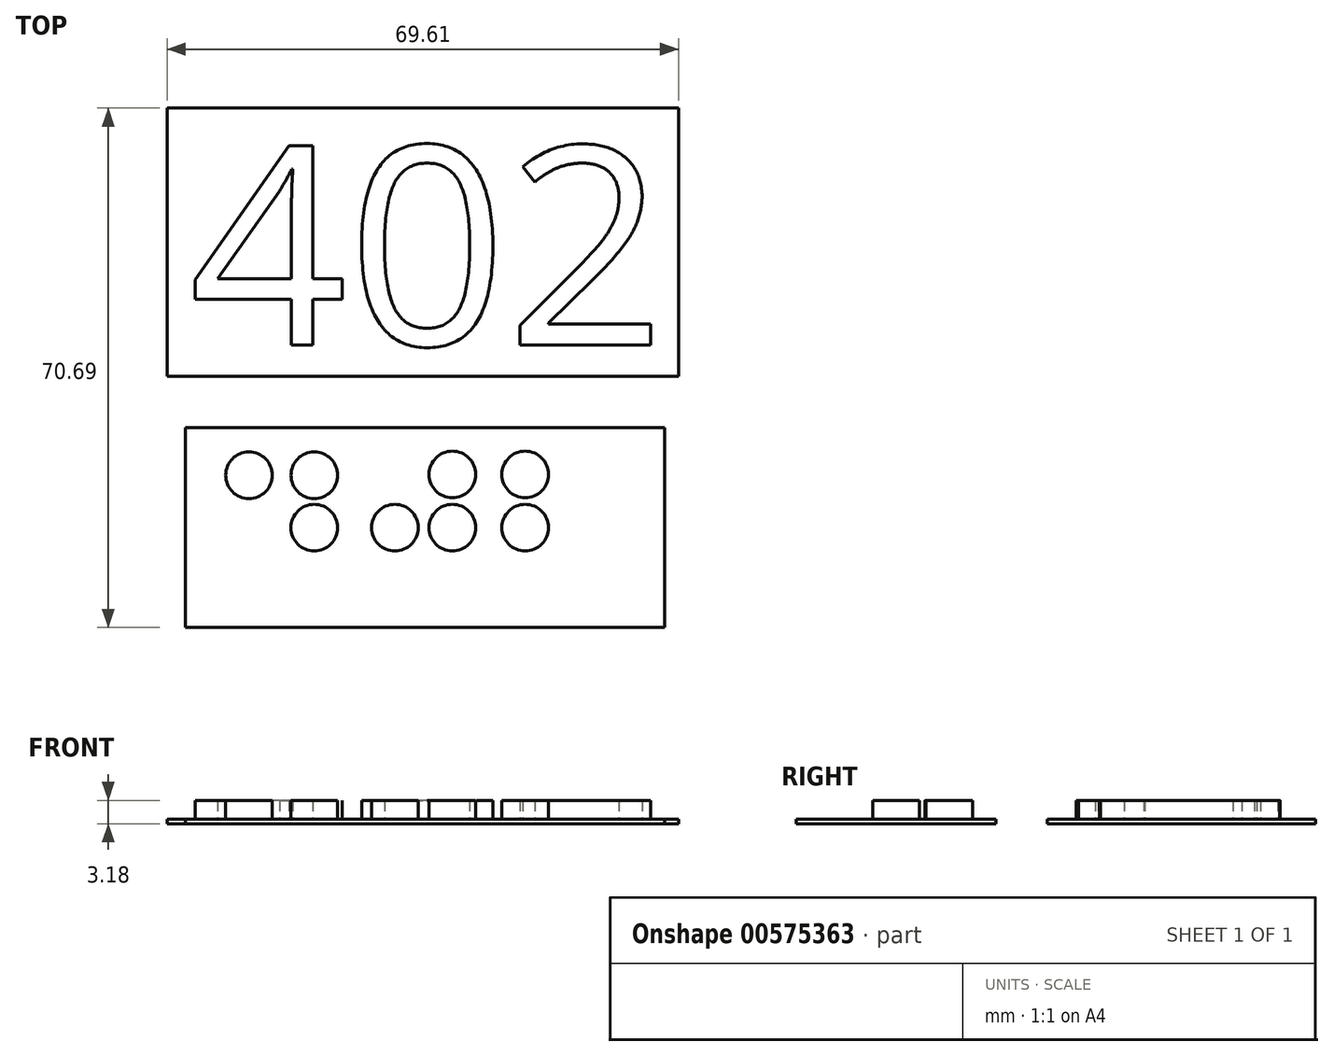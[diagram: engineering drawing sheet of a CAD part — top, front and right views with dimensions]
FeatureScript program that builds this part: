
annotation { "Feature Type Name" : "Feature", "Feature Type Description" : "" }
export const myFeature = defineFeature(function(context is Context, id is Id, definition is map)
    precondition{}
    {
        {
            var Q0;
            Q0=qCreatedBy(makeId("Top.planeOp"),FACE);
            var sketch = newSketch(context, id + "F0", { "sketchPlane" : qUnion([Q0])});
            skText(sketch, "E0", { "text": "402\n", "fontName": "OpenSans-Regular.ttf"});
            skCircle(sketch, "E1", {"center": v(-65.38, 7.14) * mm, "radius": 3.18 * mm});
            skCircle(sketch, "E2", {"center": v(-27.8, 7.24) * mm, "radius": 3.18 * mm});
            skCircle(sketch, "E3", {"center": v(-37.7, 7.24) * mm, "radius": 3.18 * mm});
            skCircle(sketch, "E4", {"center": v(-27.8, 0) * mm, "radius": 3.18 * mm});
            skCircle(sketch, "E5", {"center": v(-37.7, 0) * mm, "radius": 3.18 * mm});
            skCircle(sketch, "E6", {"center": v(-45.52, 0) * mm, "radius": 3.18 * mm});
            skCircle(sketch, "E7", {"center": v(-56.49, 7.14) * mm, "radius": 3.18 * mm});
            skCircle(sketch, "E8", {"center": v(-56.5, 0) * mm, "radius": 3.18 * mm});
            const initialGuessF0  = {"E0": [-0.07352, 0.02487, 1, 0, 0.0272]};
            skSetInitialGuess(sketch, initialGuessF0);
            skSolve(sketch);
        }
        {
            var Q0;
            Q0 = qSketchRegion(id + "F0", true);
            extrude(context, id + "F1", {"entities" : qUnion([Q0]), "depth" : 2.54 * mm, "offsetDistance" : 25.4 * mm});
        }
        {
            var Q0;
            Q0=qCreatedBy(makeId("Top.planeOp"),FACE);
            var sketch = newSketch(context, id + "F2", { "sketchPlane" : qUnion([Q0])});
            skLineSegment(sketch, "E9.bottom", {"start": v(-74.02, 13.61) * mm, "end": v(-8.79, 13.61) * mm});
            skLineSegment(sketch, "E9.top", {"start": v(-74.02, -13.59) * mm, "end": v(-8.79, -13.59) * mm});
            skLineSegment(sketch, "E9.left", {"start": v(-74.02, 13.61) * mm, "end": v(-74.02, -13.59) * mm});
            skLineSegment(sketch, "E9.right", {"start": v(-8.79, 13.61) * mm, "end": v(-8.79, -13.59) * mm});
            skLineSegment(sketch, "E10.bottom", {"start": v(-76.54, 57.1) * mm, "end": v(-6.93, 57.1) * mm});
            skLineSegment(sketch, "E10.top", {"start": v(-76.54, 20.58) * mm, "end": v(-6.93, 20.58) * mm});
            skLineSegment(sketch, "E10.left", {"start": v(-76.54, 57.1) * mm, "end": v(-76.54, 20.58) * mm});
            skLineSegment(sketch, "E10.right", {"start": v(-6.93, 57.1) * mm, "end": v(-6.93, 20.58) * mm});
            skSolve(sketch);
        }
        {
            var Q0;
            Q0 = qSketchRegion(id + "F2", true);
            extrude(context, id + "F3", {"entities" : qUnion([Q0]), "operationType" : NewBodyOperationType.ADD, "oppositeDirection" : true, "depth" : 0.64 * mm, "offsetDistance" : 25.4 * mm});
        }
    });
